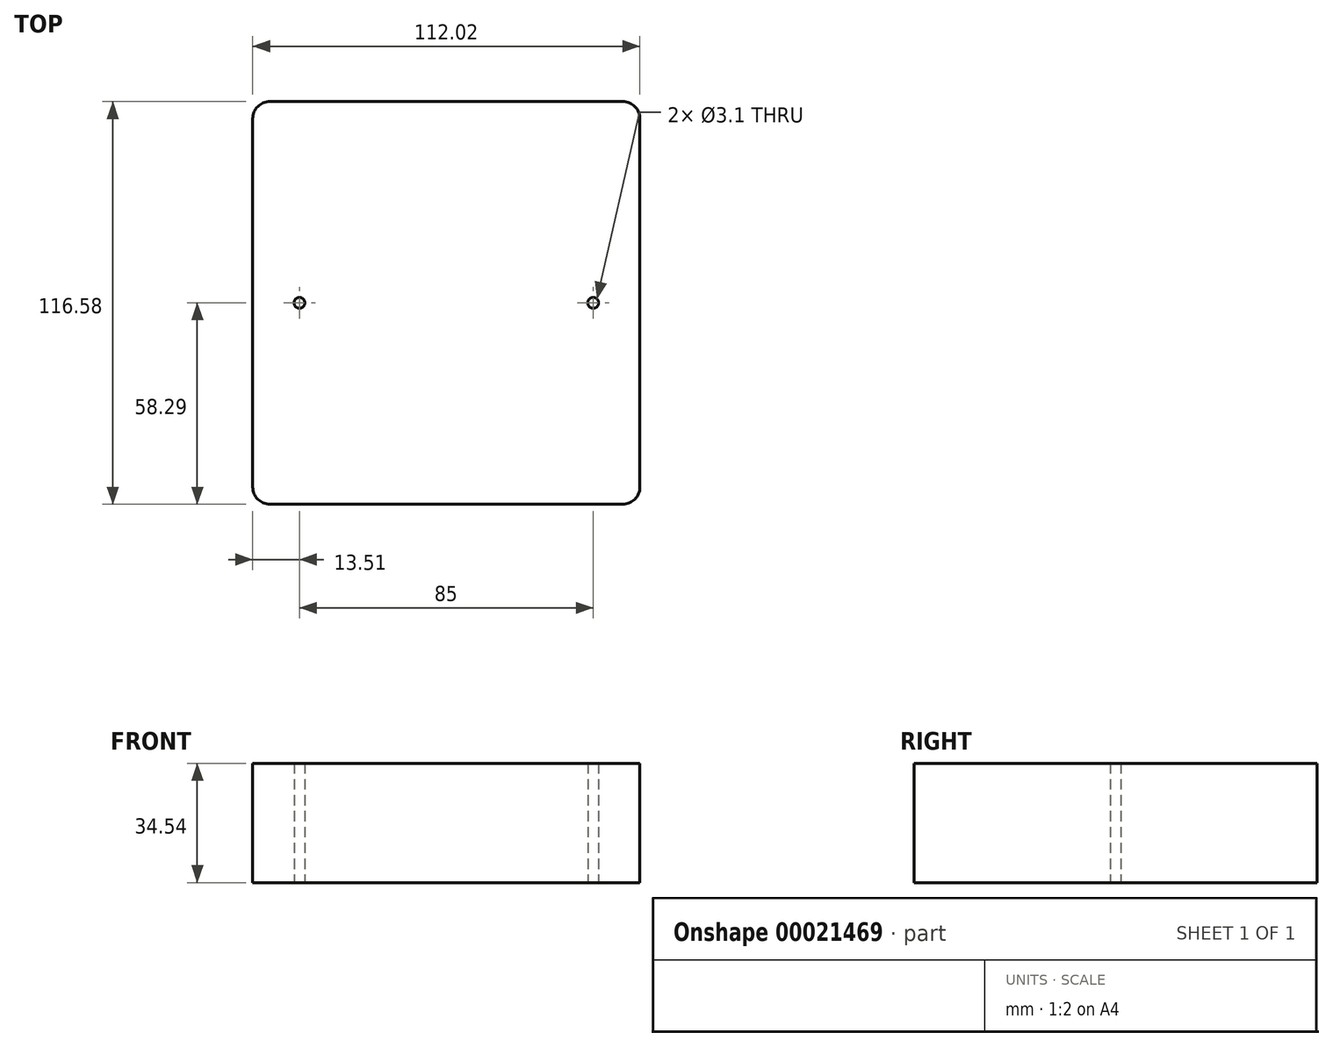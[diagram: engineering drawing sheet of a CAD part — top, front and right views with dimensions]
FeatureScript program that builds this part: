
annotation { "Feature Type Name" : "Feature", "Feature Type Description" : "" }
export const myFeature = defineFeature(function(context is Context, id is Id, definition is map)
    precondition{}
    {
        {
            var Q0;
            Q0=qCreatedBy(makeId("Top.planeOp"),FACE);
            var sketch = newSketch(context, id + "F0", { "sketchPlane" : qUnion([Q0])});
            skLineSegment(sketch, "E0.rect.bottom", {"start": v(51, -58.3) * mm, "end": v(-51, -58.3) * mm});
            skLineSegment(sketch, "E0.rect.top", {"start": v(51, 58.3) * mm, "end": v(-51, 58.3) * mm});
            skLineSegment(sketch, "E0.rect.left", {"start": v(56, -53.3) * mm, "end": v(56, 53.3) * mm});
            skLineSegment(sketch, "E0.rect.right", {"start": v(-56, -53.3) * mm, "end": v(-56, 53.3) * mm});
            skPoint(sketch, "E0.rect.middle", {"position": v(0, 0) * mm});
            skPoint(sketch, "E1.visualSharp", {"position": v(-56, -58.3) * mm});
            skArc(sketch, "E1.filletArc", {"start": v(-56, -53.3) * mm, "mid": v(-54.54, -56.83) * mm, "end": v(-51, -58.3) * mm});
            skPoint(sketch, "E2.visualSharp", {"position": v(56, -58.3) * mm});
            skArc(sketch, "E2.filletArc", {"start": v(51, -58.3) * mm, "mid": v(54.54, -56.83) * mm, "end": v(56, -53.3) * mm});
            skPoint(sketch, "E3.visualSharp", {"position": v(56, 58.3) * mm});
            skArc(sketch, "E3.filletArc", {"start": v(56, 53.3) * mm, "mid": v(54.54, 56.83) * mm, "end": v(51, 58.3) * mm});
            skPoint(sketch, "E4.visualSharp", {"position": v(-56, 58.3) * mm});
            skArc(sketch, "E4.filletArc", {"start": v(-51, 58.3) * mm, "mid": v(-54.54, 56.83) * mm, "end": v(-56, 53.3) * mm});
            skSolve(sketch);
        }
        {
            var Q0;
            Q0 = qSketchRegion(id + "F0", true);
            extrude(context, id + "F1", {"entities" : qUnion([Q0]), "depth" : 34.54 * mm});
        }
        {
            var Q0;
            Q0=makeQuery(id+"F1.opExtrude","CAP_FACE",FACE,{"disambiguationData":[OSD([sQuery(id+"F0.wireOp",EDGE,"E0.rect.bottom"),sQuery(id+"F0.wireOp",EDGE,"E0.rect.top"),sQuery(id+"F0.wireOp",EDGE,"E0.rect.left"),sQuery(id+"F0.wireOp",EDGE,"E0.rect.right")])],"isStart":true});
            var sketch = newSketch(context, id + "F2", { "sketchPlane" : qUnion([Q0])});
            skLineSegment(sketch, "E5", {"start": v(0, 41.73) * mm, "end": v(0, -43.27) * mm, "construction": true});
            skLineSegment(sketch, "E6", {"start": v(-66.02, 0) * mm, "end": v(68.2, 0) * mm, "construction": true});
            skCircle(sketch, "E7", {"center": v(-42.5, 0) * mm, "radius": 1.55 * mm});
            skCircle(sketch, "E8.MirrorC", {"center": v(42.5, 0) * mm, "radius": 1.55 * mm});
            skSolve(sketch);
        }
        {
            var Q0;
            Q0 = qSketchRegion(id + "F2", true);
            extrude(context, id + "F3", {"entities" : qUnion([Q0]), "operationType" : NewBodyOperationType.REMOVE, "endBound" : BoundingType.THROUGH_ALL, "oppositeDirection" : true, "depth" : 25 * mm});
        }
    });
